# Revit family: Genie_Site_Telehandler_GTH5519a
name_source: partatom
category: Site
revit_build: Autodesk Revit 2017 (Build: 20160225_1515(x64)
units: mm (PartAtom-declared; Revit-internal decimal feet)

## family parameters
Always vertical = Yes
Cut with Voids When Loaded = No
OmniClass Number = 23.50.85.17
OmniClass Title = Telescoping Platforms
Part Type = Normal
Round Connector Dimension = Use Diameter
Shared = No
Work Plane-Based = No

## types (1)
- GTH5519
    Assembly Code = E1030900
    AssetType = Fixed
    BIMObjectName = Genie_Site_Telehandler_GTH5519
    ClassificationName = Uniclass2015
    ClassificationValue = Pr_65_80_47_95
    Color = Grey & Blue
    Cost = 0 $
    Description = The Genie® GTH™-5519 compact telehandler is the perfect choice for tasks both large and small. Easy to maneuver and transport, and convenient to service, it meets the needs of most construction, masonry, landscape and agricultural applications.
    DocumentationLiterature = https://www.genielift.com
    DocumentationTechnical = https://www.genielift.com
    DurationUnit = Years
    ExpectedLife = 0
    Features = Comfortable, spacious cab with tilt steering and ergonomic controls, including an easy-to-use, multifunction joystick control for precise positioning, Full-time planetary four-wheel drive and four-wheel steer, Variable-speed hydrostatic drive, Manual Genie Quick-Attach™ system for a variety of attachments.
    Finish = Painted Steel
    IfcExportAs = IfcTransportElement
    IfcExportType = IfcTransportElementType
    Keynote = X
    Manufacturer = Genie
    ManufacturerName = Genie
    Material = Painted Steel
    Model = Genie - Telehandeler
    ModelNumber = GTH5519
    ModelReference = Genie - Telehandeler
    NBSDescription = Vertical lifting platforms
    NBSObjectName = Genie - Vertical lifting platforms
    NBSReference = 90-80-65/350
    NominalDepth = 1800 mm
    NominalHeight = 1980 mm
    NominalLength = 3730 mm
    ProductionYear = 2018
    ReplacementCost = 0
    Size = 1.8m x 1.98m x 3.73m
    Type Comments = GTH5519
    TypeName = Genie - Telehandeler
    URL = http://www.genielift.co.uk
    WarrantyDurationLabor = 0
    WarrantyDurationParts = 0
    WarrantyDurationUnit = Years
    WarrantyGuarantorLabor = http://www.genielift.co.uk
    WarrantyGuarantorParts = http://www.genielift.co.uk
    _BSBibleVersion = 15
    _BimSpecGuid = 0
    _CurrentRevision = 1
    _DistributedBy = www.bimstore.co.uk

## geometry (parser evidence)
native form markers: Sweep x12
no freeform markers — native parametric forms only
